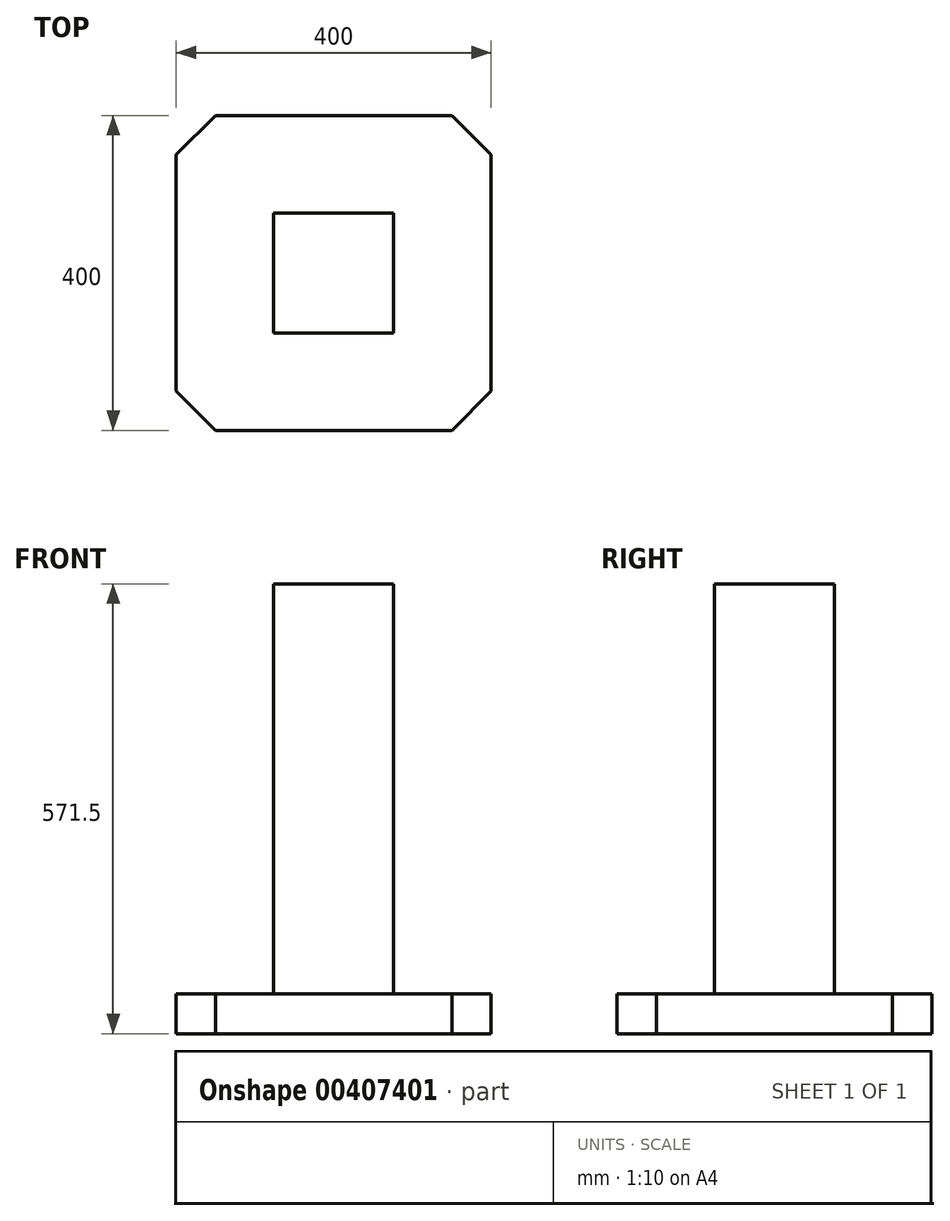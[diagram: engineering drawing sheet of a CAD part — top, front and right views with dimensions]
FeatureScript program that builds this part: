
annotation { "Feature Type Name" : "Feature", "Feature Type Description" : "" }
export const myFeature = defineFeature(function(context is Context, id is Id, definition is map)
    precondition{}
    {
        {
            var Q0;
            Q0=qCreatedBy(makeId("Top.planeOp"),FACE);
            var sketch = newSketch(context, id + "F0", { "sketchPlane" : qUnion([Q0])});
            skLineSegment(sketch, "E0.bottom", {"start": v(200, -200) * mm, "end": v(-200, -200) * mm});
            skLineSegment(sketch, "E0.top", {"start": v(200, 200) * mm, "end": v(-200, 200) * mm});
            skLineSegment(sketch, "E0.left", {"start": v(200, -200) * mm, "end": v(200, 200) * mm});
            skLineSegment(sketch, "E0.right", {"start": v(-200, -200) * mm, "end": v(-200, 200) * mm});
            skPoint(sketch, "E0.middle", {"position": v(0, 0) * mm});
            skSolve(sketch);
        }
        {
            var Q0;
            Q0=makeQuery(id+"F0.imprint","IMPRINT",FACE,{"disambiguationData":[TD([[makeQuery(id+"F0.imprint","IMPRINT",EDGE,{"derivedFrom":sQuery(id+"F0.wireOp",EDGE,"E0.bottom")}),-1.0]])]});
            extrude(context, id + "F1", {"entities" : qUnion([Q0]), "depth" : 50.8 * mm});
        }
        {
            var Q0;
            Q0=makeQuery(id+"F1.opExtrude","SWEPT_EDGE",EDGE,{"disambiguationData":[OSD([sQuery(id+"F0.wireOp",EDGE,"E0.top"),sQuery(id+"F0.wireOp",EDGE,"E0.right")])]});
            var Q1;
            Q1=makeQuery(id+"F1.opExtrude","SWEPT_EDGE",EDGE,{"disambiguationData":[OSD([sQuery(id+"F0.wireOp",EDGE,"E0.bottom"),sQuery(id+"F0.wireOp",EDGE,"E0.right")])]});
            var Q2;
            Q2=makeQuery(id+"F1.opExtrude","SWEPT_EDGE",EDGE,{"disambiguationData":[OSD([sQuery(id+"F0.wireOp",EDGE,"E0.bottom"),sQuery(id+"F0.wireOp",EDGE,"E0.left")])]});
            var Q3;
            Q3=makeQuery(id+"F1.opExtrude","SWEPT_EDGE",EDGE,{"disambiguationData":[OSD([sQuery(id+"F0.wireOp",EDGE,"E0.top"),sQuery(id+"F0.wireOp",EDGE,"E0.left")])]});
            chamfer(context, id + "F2", {"entities" : qUnion([Q0, Q1, Q2, Q3]), "width" : 50 * mm, "tangentPropagation" : true});
        }
        {
            var Q0;
            Q0=makeQuery(id+"F1.opExtrude","CAP_FACE",FACE,{"disambiguationData":[OSD([sQuery(id+"F0.wireOp",EDGE,"E0.bottom"),sQuery(id+"F0.wireOp",EDGE,"E0.top"),sQuery(id+"F0.wireOp",EDGE,"E0.left"),sQuery(id+"F0.wireOp",EDGE,"E0.right")])],"isStart":false});
            var sketch = newSketch(context, id + "F3", { "sketchPlane" : qUnion([Q0])});
            skLineSegment(sketch, "E1.bottom", {"start": v(76.2, -76.2) * mm, "end": v(-76.2, -76.2) * mm});
            skLineSegment(sketch, "E1.top", {"start": v(76.2, 76.2) * mm, "end": v(-76.2, 76.2) * mm});
            skLineSegment(sketch, "E1.left", {"start": v(76.2, -76.2) * mm, "end": v(76.2, 76.2) * mm});
            skLineSegment(sketch, "E1.right", {"start": v(-76.2, -76.2) * mm, "end": v(-76.2, 76.2) * mm});
            skPoint(sketch, "E1.middle", {"position": v(0, 0) * mm});
            skSolve(sketch);
        }
        {
            var Q0;
            Q0=qSketchRegion(id+"F3",true);
            extrude(context, id + "F4", {"entities" : qUnion([Q0]), "operationType" : NewBodyOperationType.ADD, "depth" : 520.7 * mm});
        }
    });
